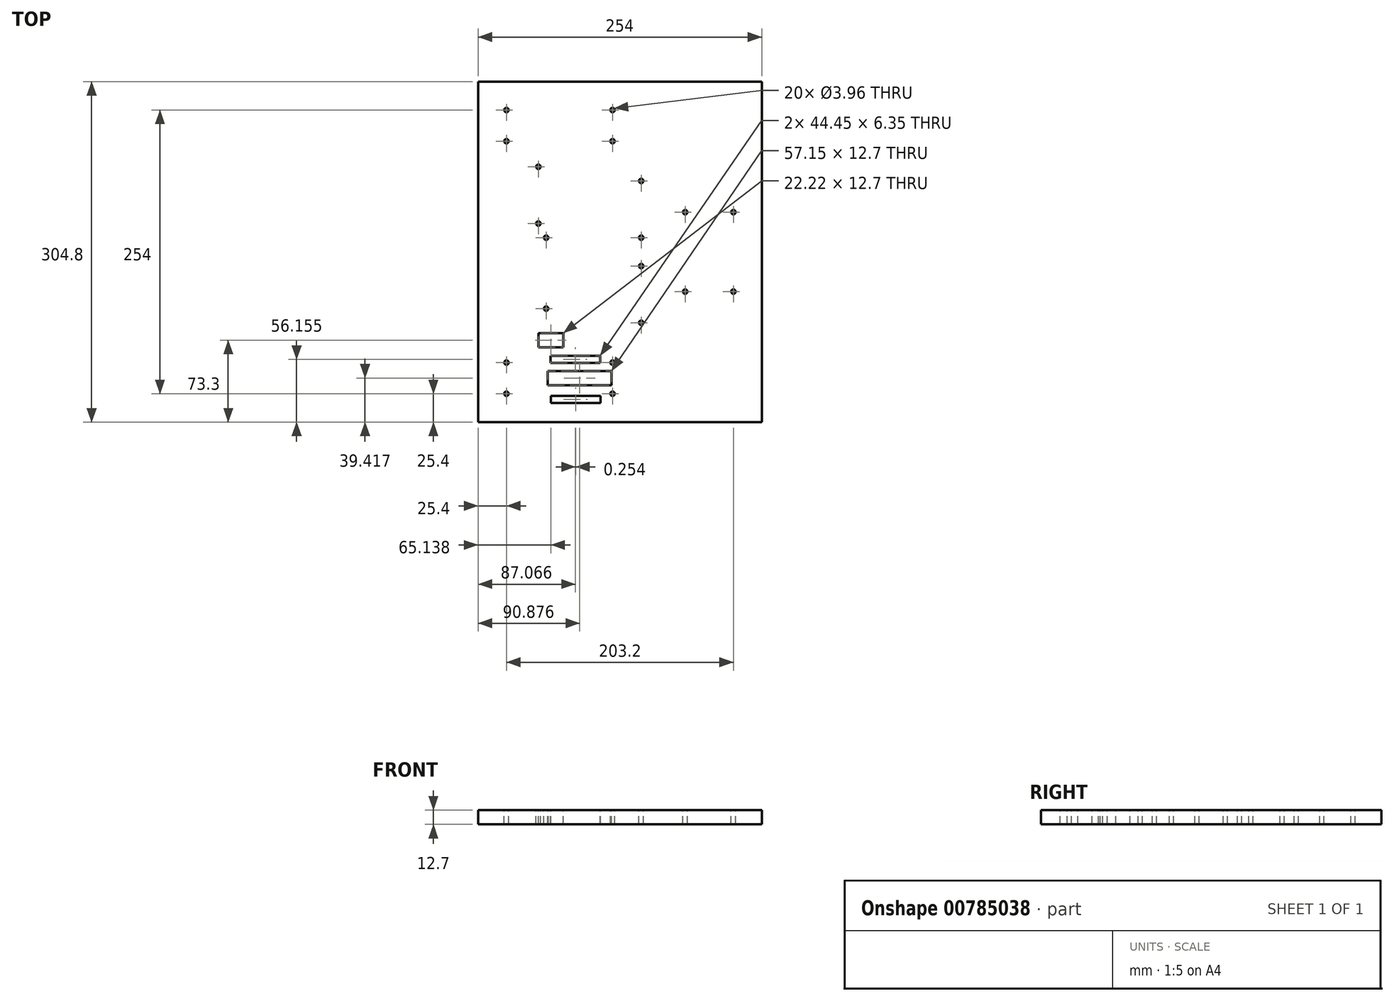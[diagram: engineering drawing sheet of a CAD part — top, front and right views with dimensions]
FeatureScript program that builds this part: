
annotation { "Feature Type Name" : "Feature", "Feature Type Description" : "" }
export const myFeature = defineFeature(function(context is Context, id is Id, definition is map)
    precondition{}
    {
        {
            var Q0;
            Q0=qCreatedBy(makeId("Top.planeOp"),FACE);
            var sketch = newSketch(context, id + "F0", { "sketchPlane" : qUnion([Q0])});
            skLineSegment(sketch, "E0.bottom", {"start": v(127, 152.4) * mm, "end": v(-127, 152.4) * mm});
            skLineSegment(sketch, "E0.top", {"start": v(127, -152.4) * mm, "end": v(-127, -152.4) * mm});
            skLineSegment(sketch, "E0.left", {"start": v(127, 152.4) * mm, "end": v(127, -152.4) * mm});
            skLineSegment(sketch, "E0.right", {"start": v(-127, 152.4) * mm, "end": v(-127, -152.4) * mm});
            skPoint(sketch, "E0.middle", {"position": v(0, 0) * mm});
            skSolve(sketch);
        }
        {
            var Q0;
            Q0=makeQuery(id+"F0.imprint","IMPRINT",FACE,{"disambiguationData":[TD([[makeQuery(id+"F0.imprint","IMPRINT",EDGE,{"derivedFrom":sQuery(id+"F0.wireOp",EDGE,"E0.bottom")}),1.0]])]});
            extrude(context, id + "F1", {"entities" : qUnion([Q0]), "depth" : 12.7 * mm, "offsetDistance" : 25.4 * mm});
        }
        {
            var Q0;
            Q0=makeQuery(id+"F1.opExtrude","CAP_FACE",FACE,{"disambiguationData":[OSD([sQuery(id+"F0.wireOp",EDGE,"E0.bottom"),sQuery(id+"F0.wireOp",EDGE,"E0.top"),sQuery(id+"F0.wireOp",EDGE,"E0.left"),sQuery(id+"F0.wireOp",EDGE,"E0.right")])],"isStart":false});
            var sketch = newSketch(context, id + "F2", { "sketchPlane" : qUnion([Q0])});
            skCircle(sketch, "E1", {"center": v(-101.6, 127) * mm, "radius": 1.98 * mm});
            skCircle(sketch, "E2", {"center": v(-101.6, 99.11) * mm, "radius": 1.98 * mm});
            skCircle(sketch, "E3", {"center": v(-6.6, 127) * mm, "radius": 1.98 * mm});
            skCircle(sketch, "E4", {"center": v(-6.6, 99.11) * mm, "radius": 1.98 * mm});
            skCircle(sketch, "E5", {"center": v(-101.6, -99.11) * mm, "radius": 1.98 * mm});
            skCircle(sketch, "E6", {"center": v(-6.6, -99.11) * mm, "radius": 1.98 * mm});
            skCircle(sketch, "E7", {"center": v(-6.6, -127) * mm, "radius": 1.98 * mm});
            skCircle(sketch, "E8", {"center": v(-101.6, -127) * mm, "radius": 1.98 * mm});
            skCircle(sketch, "E9", {"center": v(-73.02, 76.2) * mm, "radius": 1.98 * mm});
            skCircle(sketch, "E10", {"center": v(-73.02, 25.4) * mm, "radius": 1.98 * mm});
            skCircle(sketch, "E11", {"center": v(-66.04, 12.7) * mm, "radius": 1.98 * mm});
            skCircle(sketch, "E12", {"center": v(-66.04, -50.8) * mm, "radius": 1.98 * mm});
            skCircle(sketch, "E13", {"center": v(19.05, -12.7) * mm, "radius": 1.98 * mm});
            skCircle(sketch, "E14", {"center": v(19.05, -63.5) * mm, "radius": 1.98 * mm});
            skCircle(sketch, "E15", {"center": v(19.05, 63.5) * mm, "radius": 1.98 * mm});
            skCircle(sketch, "E16", {"center": v(19.05, 12.7) * mm, "radius": 1.98 * mm});
            skCircle(sketch, "E17", {"center": v(58.42, 35.56) * mm, "radius": 1.98 * mm});
            skCircle(sketch, "E18", {"center": v(101.6, 35.56) * mm, "radius": 1.98 * mm});
            skCircle(sketch, "E19", {"center": v(58.42, -35.56) * mm, "radius": 1.98 * mm});
            skCircle(sketch, "E20", {"center": v(101.6, -35.56) * mm, "radius": 1.98 * mm});
            skLineSegment(sketch, "E21.bottom", {"start": v(-64.7, -106.63) * mm, "end": v(-7.55, -106.63) * mm});
            skLineSegment(sketch, "E21.top", {"start": v(-64.7, -119.33) * mm, "end": v(-7.55, -119.33) * mm});
            skLineSegment(sketch, "E21.left", {"start": v(-64.7, -106.63) * mm, "end": v(-64.7, -119.33) * mm});
            skLineSegment(sketch, "E21.right", {"start": v(-7.55, -106.63) * mm, "end": v(-7.55, -119.33) * mm});
            skLineSegment(sketch, "E22.bottom", {"start": v(-61.9, -128.85) * mm, "end": v(-17.45, -128.85) * mm});
            skLineSegment(sketch, "E22.top", {"start": v(-61.9, -135.2) * mm, "end": v(-17.45, -135.2) * mm});
            skLineSegment(sketch, "E22.left", {"start": v(-61.9, -128.85) * mm, "end": v(-61.9, -135.2) * mm});
            skLineSegment(sketch, "E22.right", {"start": v(-17.45, -128.85) * mm, "end": v(-17.45, -135.2) * mm});
            skLineSegment(sketch, "E23.bottom", {"start": v(-72.97, -72.75) * mm, "end": v(-50.75, -72.75) * mm});
            skLineSegment(sketch, "E23.top", {"start": v(-72.97, -85.45) * mm, "end": v(-50.75, -85.45) * mm});
            skLineSegment(sketch, "E23.left", {"start": v(-72.97, -72.75) * mm, "end": v(-72.97, -85.45) * mm});
            skLineSegment(sketch, "E23.right", {"start": v(-50.75, -72.75) * mm, "end": v(-50.75, -85.45) * mm});
            skLineSegment(sketch, "E24.bottom", {"start": v(-62.16, -93.07) * mm, "end": v(-17.7, -93.07) * mm});
            skLineSegment(sketch, "E24.top", {"start": v(-62.16, -99.42) * mm, "end": v(-17.7, -99.42) * mm});
            skLineSegment(sketch, "E24.left", {"start": v(-62.16, -93.07) * mm, "end": v(-62.16, -99.42) * mm});
            skLineSegment(sketch, "E24.right", {"start": v(-17.7, -93.07) * mm, "end": v(-17.7, -99.42) * mm});
            skSolve(sketch);
        }
        {
            var Q0;
            Q0 = qSketchRegion(id + "F2", true);
            extrude(context, id + "F3", {"entities" : qUnion([Q0]), "operationType" : NewBodyOperationType.REMOVE, "oppositeDirection" : true, "depth" : 25.4 * mm, "offsetDistance" : 25.4 * mm});
        }
    });
